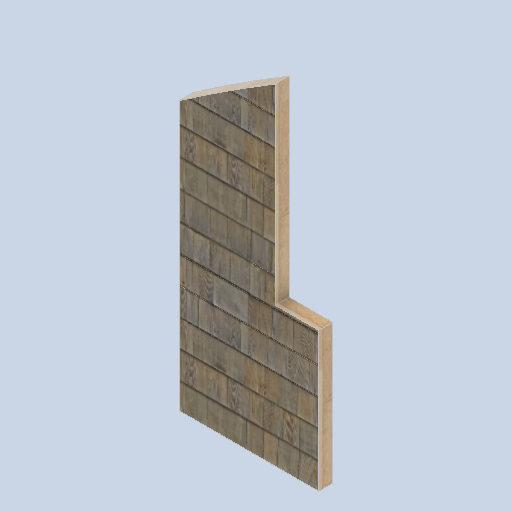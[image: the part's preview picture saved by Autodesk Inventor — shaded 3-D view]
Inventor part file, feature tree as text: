
AUTODESK INVENTOR PART (.ipt)
format: ipt  version: 2024.2 (Build 282272000, 272)  size: 195,584 bytes
history: native  units: in
note: dims shown in document units (in); Inventor stores cm internally (conversion verified against a paired STEP export)
features: other x3, sketch x1
ambient origin geometry x8: Origin, YZ Plane, XZ Plane, XY Plane, X Axis, Y Axis, Z Axis, Center Point
bodies: Solid1 (feature_tree)
feature tree (4):
  other  "front_wall_block03_MIR.ipt"
  other  "Solid1::front_wall_block03_MIR.ipt"
  other  "TaggingFeature1"
  sketch  "Sketch1"  dims[d0=0.3937in]
